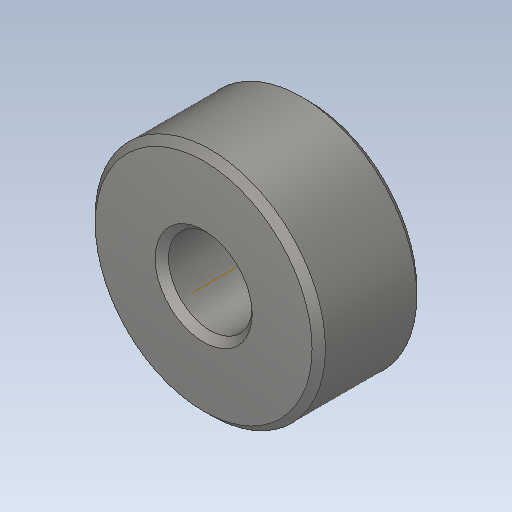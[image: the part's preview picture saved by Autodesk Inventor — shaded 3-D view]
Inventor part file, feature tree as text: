
AUTODESK INVENTOR PART (.ipt)
format: ipt  version: 2020 (Build 240168000, 168)  size: 124,928 bytes
history: native  units: in
note: dims shown in document units (in); Inventor stores cm internally (conversion verified against a paired STEP export)
features: plane x2, extrude x1, chamfer x1, sketch x1
ambient origin geometry x8: Origin, YZ Plane, XZ Plane, XY Plane, X Axis, Y Axis, Z Axis, Center Point
bodies: Solid1 (feature_tree)
feature tree (5):
  extrude  "Extrusion1"  Depth=0.125in TaperAngle=45.0deg
  chamfer  "Chamfer1"  Distance=0.25in
  plane  "Work Plane1"
  plane  "Work Plane2"
  sketch  "Sketch1"  dims[d2=0.3125in d3=0.0in d4=0.02in d5=0.125in d6=45.0deg d7=0.25in d8=0.6875in]
